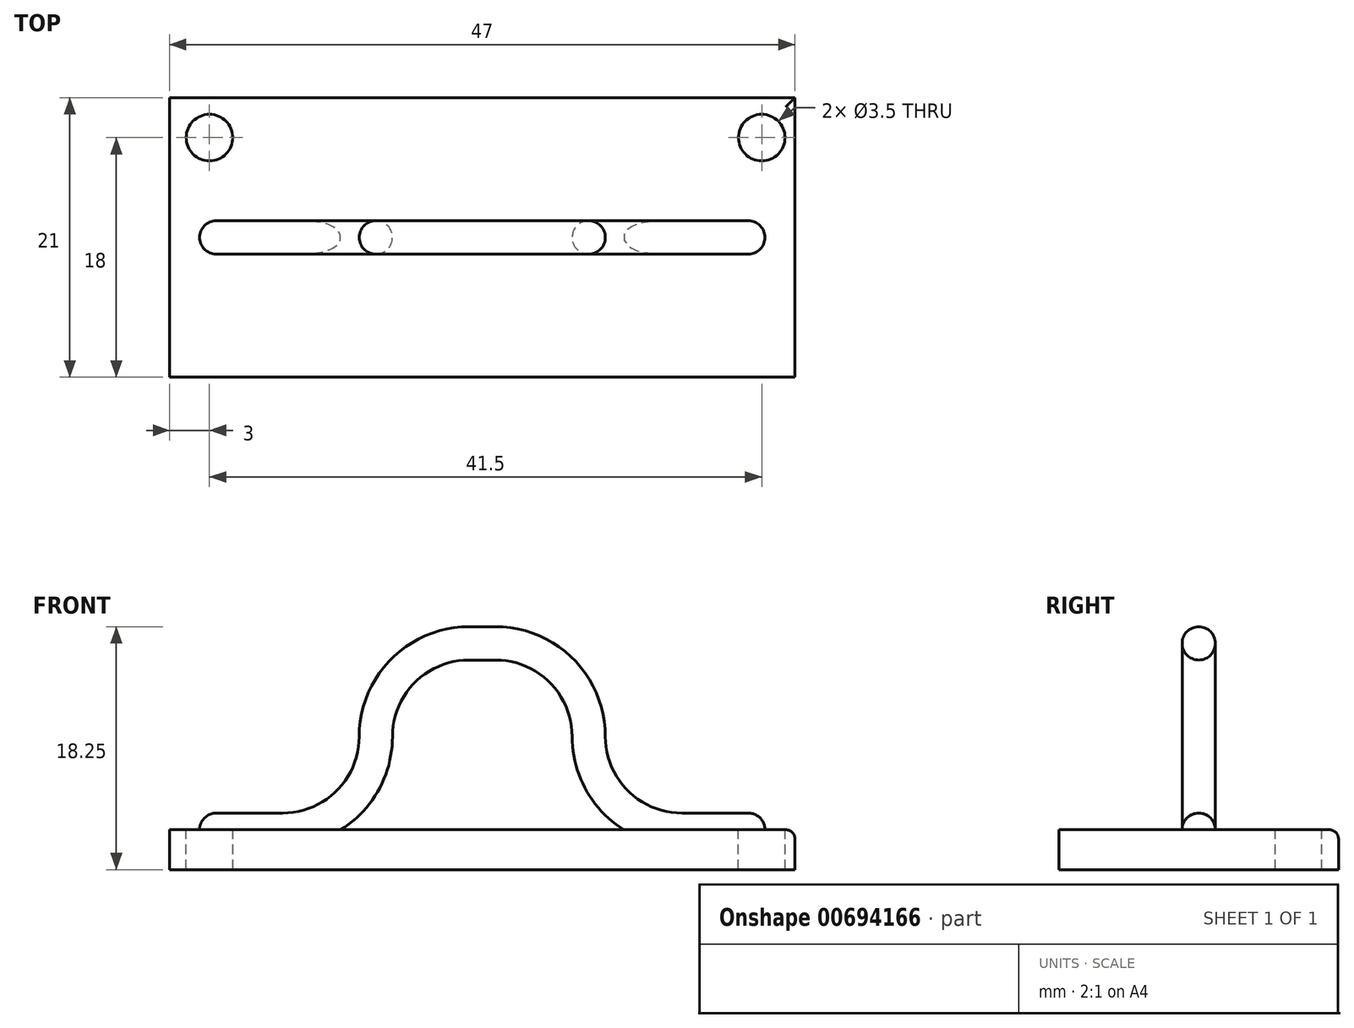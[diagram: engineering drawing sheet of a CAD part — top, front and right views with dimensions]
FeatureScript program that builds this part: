
annotation { "Feature Type Name" : "Feature", "Feature Type Description" : "" }
export const myFeature = defineFeature(function(context is Context, id is Id, definition is map)
    precondition{}
    {
        {
            var Q0;
            Q0=qCreatedBy(makeId("Top.planeOp"),FACE);
            var sketch = newSketch(context, id + "F0", { "sketchPlane" : qUnion([Q0])});
            skLineSegment(sketch, "E0.bottom", {"start": v(0, 0) * mm, "end": v(-47, 0) * mm});
            skLineSegment(sketch, "E0.top", {"start": v(0, 21) * mm, "end": v(-47, 21) * mm});
            skLineSegment(sketch, "E0.left", {"start": v(0, 0) * mm, "end": v(0, 21) * mm});
            skLineSegment(sketch, "E0.right", {"start": v(-47, 0) * mm, "end": v(-47, 21) * mm});
            skSolve(sketch);
        }
        {
            var Q0;
            Q0=makeQuery(id+"F0.imprint","IMPRINT",FACE,{"disambiguationData":[TD([[makeQuery(id+"F0.imprint","IMPRINT",EDGE,{"derivedFrom":sQuery(id+"F0.wireOp",EDGE,"E0.bottom")}),-1.0]])]});
            extrude(context, id + "F1", {"entities" : qUnion([Q0]), "depth" : 3 * mm, "offsetDistance" : 25 * mm});
        }
        {
            var Q0;
            Q0=makeQuery(id+"F1.opExtrude","CAP_FACE",FACE,{"disambiguationData":[OSD([sQuery(id+"F0.wireOp",EDGE,"E0.bottom"),sQuery(id+"F0.wireOp",EDGE,"E0.top"),sQuery(id+"F0.wireOp",EDGE,"E0.left"),sQuery(id+"F0.wireOp",EDGE,"E0.right")])],"isStart":false});
            var sketch = newSketch(context, id + "F2", { "sketchPlane" : qUnion([Q0])});
            skLineSegment(sketch, "E1", {"start": v(0, 0) * mm, "end": v(0, 21) * mm, "construction": true});
            skLineSegment(sketch, "E2", {"start": v(0, 21) * mm, "end": v(-2.5, 21) * mm, "construction": true});
            skLineSegment(sketch, "E3", {"start": v(-2.5, 21) * mm, "end": v(-2.5, 18) * mm, "construction": true});
            skLineSegment(sketch, "E4", {"start": v(-2.5, 18) * mm, "end": v(0, 18) * mm, "construction": true});
            skCircle(sketch, "E5", {"center": v(-2.5, 18) * mm, "radius": 1.75 * mm});
            skLineSegment(sketch, "E6", {"start": v(-2.5, 21) * mm, "end": v(-47, 21) * mm, "construction": true});
            skLineSegment(sketch, "E7", {"start": v(-47, 21) * mm, "end": v(-47, 18) * mm, "construction": true});
            skLineSegment(sketch, "E8", {"start": v(-47, 18) * mm, "end": v(-44, 18) * mm, "construction": true});
            skLineSegment(sketch, "E9", {"start": v(-44, 18) * mm, "end": v(-44, 21) * mm, "construction": true});
            skCircle(sketch, "E10", {"center": v(-44, 18) * mm, "radius": 1.75 * mm});
            skSolve(sketch);
        }
        {
            var Q0;
            Q0 = qSketchRegion(id + "F2", true);
            extrude(context, id + "F3", {"entities" : qUnion([Q0]), "operationType" : NewBodyOperationType.REMOVE, "oppositeDirection" : true, "depth" : 5 * mm, "offsetDistance" : 25 * mm});
        }
        {
            var Q0;
            Q0=qCreatedBy(makeId("Top.planeOp"),FACE);
            cPlane(context, id + "F4", {"entities" : qUnion([Q0]), "cplaneType" : CPlaneType.OFFSET, "offset" : 1.75 * mm, "width" : 150 * mm, "height" : 150 * mm});
        }
        {
            var Q0;
            Q0=qCreatedBy(makeId("Right.planeOp"),FACE);
            cPlane(context, id + "F5", {"entities" : qUnion([Q0]), "cplaneType" : CPlaneType.OFFSET, "offset" : 3.5 * mm, "oppositeDirection" : true, "width" : 150 * mm, "height" : 150 * mm});
        }
        {
            var Q0;
            Q0=qCreatedBy(id+"F5.planeOp",FACE);
            var sketch = newSketch(context, id + "F6", { "sketchPlane" : qUnion([Q0])});
            skLineSegment(sketch, "E11", {"start": v(0, 0) * mm, "end": v(10.5, 0) * mm, "construction": true});
            skLineSegment(sketch, "E12", {"start": v(10.5, 0) * mm, "end": v(10.5, 1.76) * mm, "construction": true});
            skLineSegment(sketch, "E13", {"start": v(10.5, 1.76) * mm, "end": v(10.5, 3) * mm, "construction": true});
            skCircle(sketch, "E14", {"center": v(10.5, 3) * mm, "radius": 1.25 * mm});
            skSolve(sketch);
        }
        {
            var Q0;
            Q0=qCreatedBy(makeId("Front.planeOp"),FACE);
            cPlane(context, id + "F7", {"entities" : qUnion([Q0]), "cplaneType" : CPlaneType.OFFSET, "offset" : 10.5 * mm, "oppositeDirection" : true, "width" : 150 * mm, "height" : 150 * mm});
        }
        {
            var Q0;
            Q0=makeQuery(id+"F6.imprint","IMPRINT",FACE,{"disambiguationData":[TD([[makeQuery(id+"F6.imprint","IMPRINT",EDGE,{"derivedFrom":sQuery(id+"F6.wireOp",EDGE,"E14")}),1.0]])]});
            extrude(context, id + "F8", {"entities" : qUnion([Q0]), "oppositeDirection" : true, "depth" : 5 * mm, "offsetDistance" : 25 * mm});
        }
        {
            var Q0;
            Q0=qCreatedBy(makeId("Top.planeOp"),FACE);
            cPlane(context, id + "F9", {"entities" : qUnion([Q0]), "cplaneType" : CPlaneType.OFFSET, "offset" : 10 * mm, "width" : 150 * mm, "height" : 150 * mm});
        }
        {
            var Q0;
            Q0=qCreatedBy(id+"F9.planeOp",FACE);
            var sketch = newSketch(context, id + "F10", { "sketchPlane" : qUnion([Q0])});
            skLineSegment(sketch, "E15", {"start": v(0, 0) * mm, "end": v(0, 10.5) * mm, "construction": true});
            skLineSegment(sketch, "E16", {"start": v(0, 10.5) * mm, "end": v(-15.5, 10.5) * mm, "construction": true});
            skCircle(sketch, "E17", {"center": v(-15.5, 10.5) * mm, "radius": 1.25 * mm});
            skSolve(sketch);
        }
        {
            var Q0;
            Q0=qCreatedBy(id+"F7.planeOp",FACE);
            var sketch = newSketch(context, id + "F11", { "sketchPlane" : qUnion([Q0])});
            skLineSegment(sketch, "E18", {"start": v(0, 0) * mm, "end": v(0, 3) * mm, "construction": true});
            skLineSegment(sketch, "E19", {"start": v(0, 3) * mm, "end": v(-8.5, 3) * mm, "construction": true});
            skLineSegment(sketch, "E20", {"start": v(-8.5, 3) * mm, "end": v(-11.75, 3) * mm, "construction": true});
            skLineSegment(sketch, "E21", {"start": v(-11.75, 6.25) * mm, "end": v(-8.5, 6.25) * mm, "construction": true});
            skLineSegment(sketch, "E22", {"start": v(-8.5, 6.25) * mm, "end": v(-8.5, 3) * mm, "construction": true});
            skLineSegment(sketch, "E23", {"start": v(-11.75, 10) * mm, "end": v(-11.75, 12.25) * mm});
            skLineSegment(sketch, "E24", {"start": v(-15, 15.5) * mm, "end": v(-15, 3) * mm, "construction": true});
            skLineSegment(sketch, "E25", {"start": v(-11.75, 12.25) * mm, "end": v(-15, 12.25) * mm, "construction": true});
            skLineSegment(sketch, "E26", {"start": v(-11.75, 3) * mm, "end": v(-15, 3) * mm, "construction": true});
            skLineSegment(sketch, "E27", {"start": v(-15, 3) * mm, "end": v(-15, 10) * mm, "construction": true});
            skLineSegment(sketch, "E28", {"start": v(-15, 10) * mm, "end": v(-11.75, 10) * mm, "construction": true});
            skLineSegment(sketch, "E29", {"start": v(-11.75, 10) * mm, "end": v(-8.5, 10) * mm, "construction": true});
            skArc(sketch, "E30", {"start": v(-8.5, 3) * mm, "mid": v(-13.45, 5.05) * mm, "end": v(-15.5, 10) * mm});
            skLineSegment(sketch, "E31", {"start": v(-15.5, 10) * mm, "end": v(-11.82, 10) * mm, "construction": true});
            skLineSegment(sketch, "E32", {"start": v(-15.5, 10) * mm, "end": v(-22.5, 10) * mm, "construction": true});
            skLineSegment(sketch, "E33", {"start": v(-22.5, 10) * mm, "end": v(-22.5, 17) * mm, "construction": true});
            skArc(sketch, "E34", {"start": v(-15.5, 10) * mm, "mid": v(-17.55, 14.95) * mm, "end": v(-22.5, 17) * mm});
            skPoint(sketch, "E35.end.orphan", {"position": v(-11.75, 15.5) * mm});
            skSolve(sketch);
        }
        {
            var Q0;
            Q0=makeQuery(id+"F10.imprint","IMPRINT",FACE,{"disambiguationData":[TD([[makeQuery(id+"F10.imprint","IMPRINT",EDGE,{"derivedFrom":sQuery(id+"F10.wireOp",EDGE,"E17")}),1.0]])]});
            var Q1;
            Q1=sQuery(id+"F11.wireOp",EDGE,"E30");
            var Q2;
            Q2=sQuery(id+"F11.wireOp",EDGE,"E34");
            sweep(context, id + "F12", {"profiles" : qUnion([Q0]), "path" : qUnion([Q1, Q2])});
        }
        {
            var Q0;
            Q0=qCreatedBy(makeId("Right.planeOp"),FACE);
            cPlane(context, id + "F13", {"entities" : qUnion([Q0]), "cplaneType" : CPlaneType.OFFSET, "offset" : 23.5 * mm, "oppositeDirection" : true, "width" : 150 * mm, "height" : 150 * mm});
        }
        {
            var Q0;
            Q0=makeQuery(id+"F12.opSweep","SWEPT_BODY",BODY,{"disambiguationData":[OSD([sQuery(id+"F10.wireOp",EDGE,"E17"),sQuery(id+"F11.wireOp",EDGE,"E34")])]});
            var Q1;
            Q1=makeQuery(id+"F8.opExtrude","SWEPT_BODY",BODY,{"disambiguationData":[OSD([sQuery(id+"F6.wireOp",EDGE,"E14")])]});
            var Q2;
            Q2=qCreatedBy(id+"F13.planeOp",FACE);
            mirror(context, id + "F14", {"operationType" : NewBodyOperationType.ADD, "entities" : qUnion([Q0, Q1]), "mirrorPlane" : qUnion([Q2])});
        }
        {
            var Q0;
            Q0=makeQuery(id+"F8.opExtrude","CAP_FACE",FACE,{"disambiguationData":[OSD([sQuery(id+"F6.wireOp",EDGE,"E14")])],"isStart":true});
            var Q1;
            Q1=makeQuery(id+"F14.boolean.opBoolean","INTERSECT",EDGE,{"derivedFrom":[makeQuery(id+"F1.opExtrude","CAP_FACE",FACE,{"disambiguationData":[OSD([sQuery(id+"F0.wireOp",EDGE,"E0.bottom"),sQuery(id+"F0.wireOp",EDGE,"E0.top"),sQuery(id+"F0.wireOp",EDGE,"E0.left"),sQuery(id+"F0.wireOp",EDGE,"E0.right")])],"isStart":false}),makeQuery(id+"F8.opExtrude","CAP_FACE",FACE,{"disambiguationData":[OSD([sQuery(id+"F6.wireOp",EDGE,"E14")])],"isStart":true})]});
            revolve(context, id + "F15", {"operationType" : NewBodyOperationType.ADD, "entities" : qUnion([Q0]), "axis" : qUnion([Q1]), "revolveType" : RevolveType.FULL});
        }
        {
            var Q0;
            Q0=makeQuery(id+"F14.opPattern","COPY",FACE,{"derivedFrom":makeQuery(id+"F8.opExtrude","CAP_FACE",FACE,{"disambiguationData":[OSD([sQuery(id+"F6.wireOp",EDGE,"E14")])],"isStart":true}),"instanceName":"1"});
            var Q1;
            Q1=makeQuery(id+"F14.boolean.opBoolean","INTERSECT",EDGE,{"derivedFrom":[makeQuery(id+"F1.opExtrude","CAP_FACE",FACE,{"disambiguationData":[OSD([sQuery(id+"F0.wireOp",EDGE,"E0.bottom"),sQuery(id+"F0.wireOp",EDGE,"E0.top"),sQuery(id+"F0.wireOp",EDGE,"E0.left"),sQuery(id+"F0.wireOp",EDGE,"E0.right")])],"isStart":false}),makeQuery(id+"F14.opPattern","COPY",FACE,{"derivedFrom":makeQuery(id+"F8.opExtrude","CAP_FACE",FACE,{"disambiguationData":[OSD([sQuery(id+"F6.wireOp",EDGE,"E14")])],"isStart":true}),"instanceName":"1"})]});
            revolve(context, id + "F16", {"operationType" : NewBodyOperationType.ADD, "entities" : qUnion([Q0]), "axis" : qUnion([Q1]), "revolveType" : RevolveType.FULL});
        }
        {
            var Q0;
            Q0=makeQuery(id+"F14.opPattern","COPY",FACE,{"derivedFrom":makeQuery(id+"F12.opSweep","CAP_FACE",FACE,{"disambiguationData":[OSD([sQuery(id+"F10.wireOp",EDGE,"E17"),sQuery(id+"F11.wireOp",VERTEX,"E34.end")])],"isStart":false}),"instanceName":"1"});
            extrude(context, id + "F17", {"entities" : qUnion([Q0]), "operationType" : NewBodyOperationType.ADD, "depth" : 2 * mm, "offsetDistance" : 25 * mm});
        }
        {
            var Q0;
            Q0=makeQuery(id+"F1.opExtrude","CAP_EDGE",EDGE,{"disambiguationData":[OSD([sQuery(id+"F0.wireOp",EDGE,"E0.left")])],"isStart":false});
            var Q1;
            Q1=makeQuery(id+"F1.opExtrude","CAP_EDGE",EDGE,{"disambiguationData":[OSD([sQuery(id+"F0.wireOp",EDGE,"E0.top")])],"isStart":false});
            fillet(context, id + "F18", {"entities" : qUnion([Q0, Q1]), "radius" : 0.7 * mm, "tangentPropagation" : true, "allowEdgeOverflow" : false});
        }
    });
